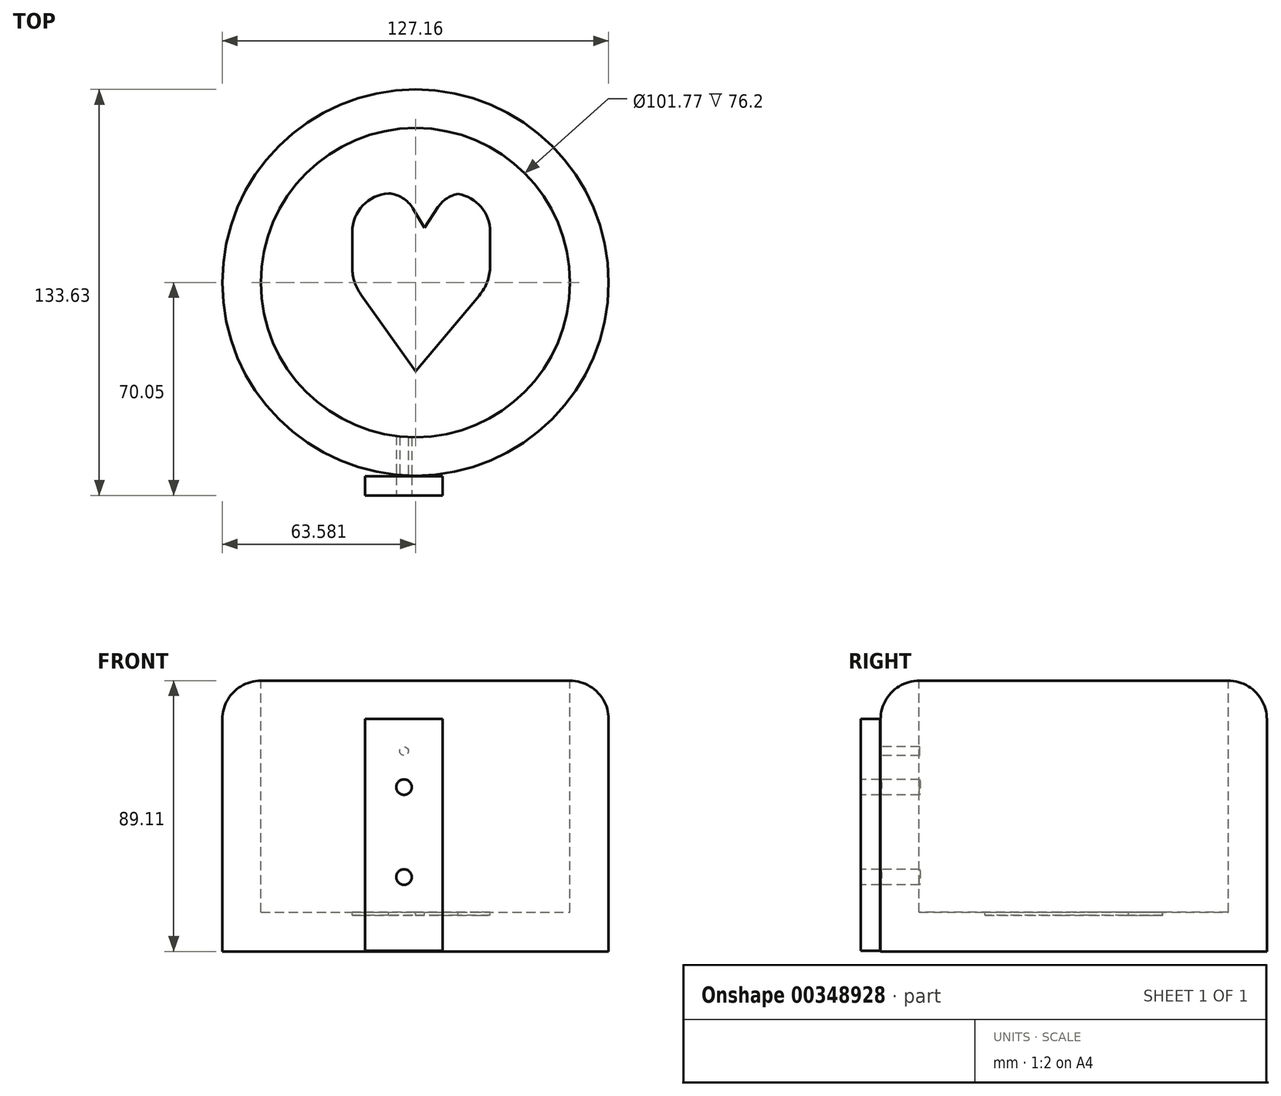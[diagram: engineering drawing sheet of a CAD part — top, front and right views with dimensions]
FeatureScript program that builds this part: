
annotation { "Feature Type Name" : "Feature", "Feature Type Description" : "" }
export const myFeature = defineFeature(function(context is Context, id is Id, definition is map)
    precondition{}
    {
        {
            var Q0;
            Q0=qCreatedBy(makeId("Front.planeOp"),FACE);
            var sketch = newSketch(context, id + "F0", { "sketchPlane" : qUnion([Q0])});
            skLineSegment(sketch, "E0", {"start": v(3.77, 45.5) * mm, "end": v(54.65, 45.5) * mm});
            skLineSegment(sketch, "E1", {"start": v(67.35, 32.8) * mm, "end": v(67.35, -43.6) * mm});
            skLineSegment(sketch, "E2", {"start": v(67.35, -43.6) * mm, "end": v(3.77, -43.6) * mm});
            skLineSegment(sketch, "E3", {"start": v(3.77, -43.6) * mm, "end": v(3.77, 45.5) * mm});
            skPoint(sketch, "E4.visualSharp", {"position": v(67.35, 45.5) * mm});
            skArc(sketch, "E4.filletArc", {"start": v(67.35, 32.8) * mm, "mid": v(63.63, 41.78) * mm, "end": v(54.65, 45.5) * mm});
            skSolve(sketch);
        }
        {
            var Q0;
            Q0=makeQuery(id+"F0.imprint","IMPRINT",FACE,{"disambiguationData":[TD([[makeQuery(id+"F0.imprint","IMPRINT",EDGE,{"derivedFrom":sQuery(id+"F0.wireOp",EDGE,"E0")}),-1.0]])]});
            var Q1;
            Q1=sQuery(id+"F0.wireOp",EDGE,"E3");
            revolve(context, id + "F1", {"entities" : qUnion([Q0]), "axis" : qUnion([Q1]), "revolveType" : RevolveType.FULL});
        }
        {
            var Q0;
            Q0=makeQuery(id+"F1.opRevolve","SWEPT_FACE",FACE,{"disambiguationData":[OSD([sQuery(id+"F0.wireOp",EDGE,"E0")])]});
            extrude(context, id + "F2", {"entities" : qUnion([Q0]), "operationType" : NewBodyOperationType.REMOVE, "oppositeDirection" : true, "depth" : 76.2 * mm});
        }
        {
            var Q0;
            Q0=qCreatedBy(makeId("Front.planeOp"),FACE);
            cPlane(context, id + "F3", {"entities" : qUnion([Q0]), "cplaneType" : CPlaneType.OFFSET, "offset" : 63.7 * mm, "width" : 152.4 * mm, "height" : 152.4 * mm});
        }
        {
            var Q0;
            Q0=qCreatedBy(id+"F3.planeOp",FACE);
            var sketch = newSketch(context, id + "F4", { "sketchPlane" : qUnion([Q0])});
            skLineSegment(sketch, "E5.bottom", {"start": v(-12.76, 32.97) * mm, "end": v(12.76, 32.97) * mm});
            skLineSegment(sketch, "E5.top", {"start": v(-12.76, -43.37) * mm, "end": v(12.76, -43.37) * mm});
            skLineSegment(sketch, "E5.left", {"start": v(-12.76, 32.97) * mm, "end": v(-12.76, -43.37) * mm});
            skLineSegment(sketch, "E5.right", {"start": v(12.76, 32.97) * mm, "end": v(12.76, -43.37) * mm});
            skSolve(sketch);
        }
        {
            var Q0;
            Q0=makeQuery(id+"F4.imprint","IMPRINT",FACE,{"disambiguationData":[TD([[makeQuery(id+"F4.imprint","IMPRINT",EDGE,{"derivedFrom":sQuery(id+"F4.wireOp",EDGE,"E5.bottom")}),-1.0]])]});
            extrude(context, id + "F5", {"entities" : qUnion([Q0]), "depth" : 6.35 * mm});
        }
        {
            var Q0;
            Q0=qCreatedBy(id+"F3.planeOp",FACE);
            var sketch = newSketch(context, id + "F6", { "sketchPlane" : qUnion([Q0])});
            skCircle(sketch, "E6", {"center": v(0, 22.34) * mm, "radius": 1.44 * mm});
            skSolve(sketch);
        }
        {
            var Q0;
            Q0 = qSketchRegion(id + "F6", true);
            extrude(context, id + "F7", {"entities" : qUnion([Q0]), "operationType" : NewBodyOperationType.REMOVE, "oppositeDirection" : true, "depth" : 25.4 * mm});
        }
        {
            var Q0;
            Q0=makeQuery(id+"F5.opExtrude","CAP_FACE",FACE,{"disambiguationData":[OSD([sQuery(id+"F4.wireOp",EDGE,"E5.bottom"),sQuery(id+"F4.wireOp",EDGE,"E5.top"),sQuery(id+"F4.wireOp",EDGE,"E5.left"),sQuery(id+"F4.wireOp",EDGE,"E5.right")])],"isStart":false});
            var sketch = newSketch(context, id + "F8", { "sketchPlane" : qUnion([Q0])});
            skPoint(sketch, "E7", {"position": v(0, 10.46) * mm});
            skPoint(sketch, "E8", {"position": v(0, -19.13) * mm});
            skSolve(sketch);
        }
        {
            var Q0;
            Q0=sQuery(id+"F8.wireOp",VERTEX,"E7");
            var Q1;
            Q1=sQuery(id+"F8.wireOp",VERTEX,"E8");
            var Q2;
            Q2=makeQuery(id+"F1.opRevolve","SWEPT_BODY",BODY,{"disambiguationData":[OSD([sQuery(id+"F0.wireOp",EDGE,"E0"),sQuery(id+"F0.wireOp",EDGE,"E1"),sQuery(id+"F0.wireOp",EDGE,"E2"),sQuery(id+"F0.wireOp",EDGE,"E3"),sQuery(id+"F0.wireOp",EDGE,"E4.filletArc")])]});
            var Q3;
            Q3=makeQuery(id+"F5.opExtrude","SWEPT_BODY",BODY,{"disambiguationData":[OSD([sQuery(id+"F4.wireOp",EDGE,"E5.bottom"),sQuery(id+"F4.wireOp",EDGE,"E5.top"),sQuery(id+"F4.wireOp",EDGE,"E5.left"),sQuery(id+"F4.wireOp",EDGE,"E5.right")])]});
            hole(context, id + "F9", {"style" : HoleStyle.SIMPLE, "endStyle" : HoleEndStyle.BLIND, "standardTappedOrClearance" : lookupTablePath({ "standard" : "ANSI", "fit" : "Normal (ASME)", "size" : "#10", "type" : "Clearance" }), "standardBlindInLast" : lookupTablePath({ "fit" : "Free", "standard" : "ANSI", "size" : "#10", "type" : "Clearance" }), "holeDiameter" : 5.1 * mm, "holeDepth" : 38.1 * mm, "isTappedThrough" : true, "tappedDepth" : 12.7 * mm, "tapClearance" : 3, "locations" : qUnion([Q0, Q1]), "scope" : qUnion([Q2, Q3])});
        }
        {
            var Q0;
            Q0=qCreatedBy(makeId("Top.planeOp"),FACE);
            cPlane(context, id + "F10", {"entities" : qUnion([Q0]), "cplaneType" : CPlaneType.OFFSET, "offset" : 25.4 * mm, "oppositeDirection" : true, "width" : 152.4 * mm, "height" : 152.4 * mm});
        }
        {
            var Q0;
            Q0=qCreatedBy(id+"F10.planeOp",FACE);
            var sketch = newSketch(context, id + "F11", { "sketchPlane" : qUnion([Q0])});
            skLineSegment(sketch, "E9", {"start": v(3.78, -29.2) * mm, "end": v(24.78, -4.25) * mm});
            skLineSegment(sketch, "E10", {"start": v(28.36, 5.56) * mm, "end": v(28.36, 16.68) * mm});
            skLineSegment(sketch, "E11", {"start": v(19.67, 29.38) * mm, "end": v(15.66, 29.38) * mm});
            skLineSegment(sketch, "E12", {"start": v(11.22, 24.86) * mm, "end": v(6.68, 18.06) * mm});
            skLineSegment(sketch, "E13", {"start": v(6.68, 18.06) * mm, "end": v(2.95, 24.39) * mm});
            skLineSegment(sketch, "E14", {"start": v(-4.32, 29.38) * mm, "end": v(-5.8, 29.38) * mm});
            skLineSegment(sketch, "E15", {"start": v(-17.02, 16.68) * mm, "end": v(-17.02, 4.87) * mm});
            skLineSegment(sketch, "E16", {"start": v(-14.19, -3.97) * mm, "end": v(3.78, -29.2) * mm});
            skPoint(sketch, "E17.visualSharp", {"position": v(28.36, 29.38) * mm});
            skArc(sketch, "E17.filletArc", {"start": v(28.36, 16.68) * mm, "mid": v(24.64, 25.66) * mm, "end": v(15.66, 29.38) * mm});
            skPoint(sketch, "E18.visualSharp", {"position": v(-17.02, 29.38) * mm});
            skArc(sketch, "E18.filletArc", {"start": v(-4.32, 29.38) * mm, "mid": v(-13.3, 25.66) * mm, "end": v(-17.02, 16.68) * mm});
            skPoint(sketch, "E19.visualSharp", {"position": v(-17.02, 0) * mm});
            skArc(sketch, "E19.filletArc", {"start": v(-17.02, 4.87) * mm, "mid": v(-16.3, 0.23) * mm, "end": v(-14.19, -3.97) * mm});
            skPoint(sketch, "E20.visualSharp", {"position": v(28.36, 0) * mm});
            skArc(sketch, "E20.filletArc", {"start": v(24.78, -4.25) * mm, "mid": v(27.44, 0.34) * mm, "end": v(28.36, 5.56) * mm});
            skPoint(sketch, "E21.visualSharp", {"position": v(0, 29.38) * mm});
            skArc(sketch, "E21.filletArc", {"start": v(2.95, 24.39) * mm, "mid": v(-0.76, 28.05) * mm, "end": v(-5.8, 29.38) * mm});
            skPoint(sketch, "E22.visualSharp", {"position": v(14.23, 29.38) * mm});
            skArc(sketch, "E22.filletArc", {"start": v(19.67, 29.38) * mm, "mid": v(14.88, 28.18) * mm, "end": v(11.22, 24.86) * mm});
            skSolve(sketch);
        }
        {
            var Q0;
            Q0=makeQuery(id+"F11.imprint","IMPRINT",FACE,{"disambiguationData":[TD([[makeQuery(id+"F11.imprint","IMPRINT",EDGE,{"derivedFrom":sQuery(id+"F11.wireOp",EDGE,"E9")}),1.0]])]});
            extrude(context, id + "F12", {"entities" : qUnion([Q0]), "operationType" : NewBodyOperationType.REMOVE, "oppositeDirection" : true, "depth" : 6.35 * mm});
        }
    });
